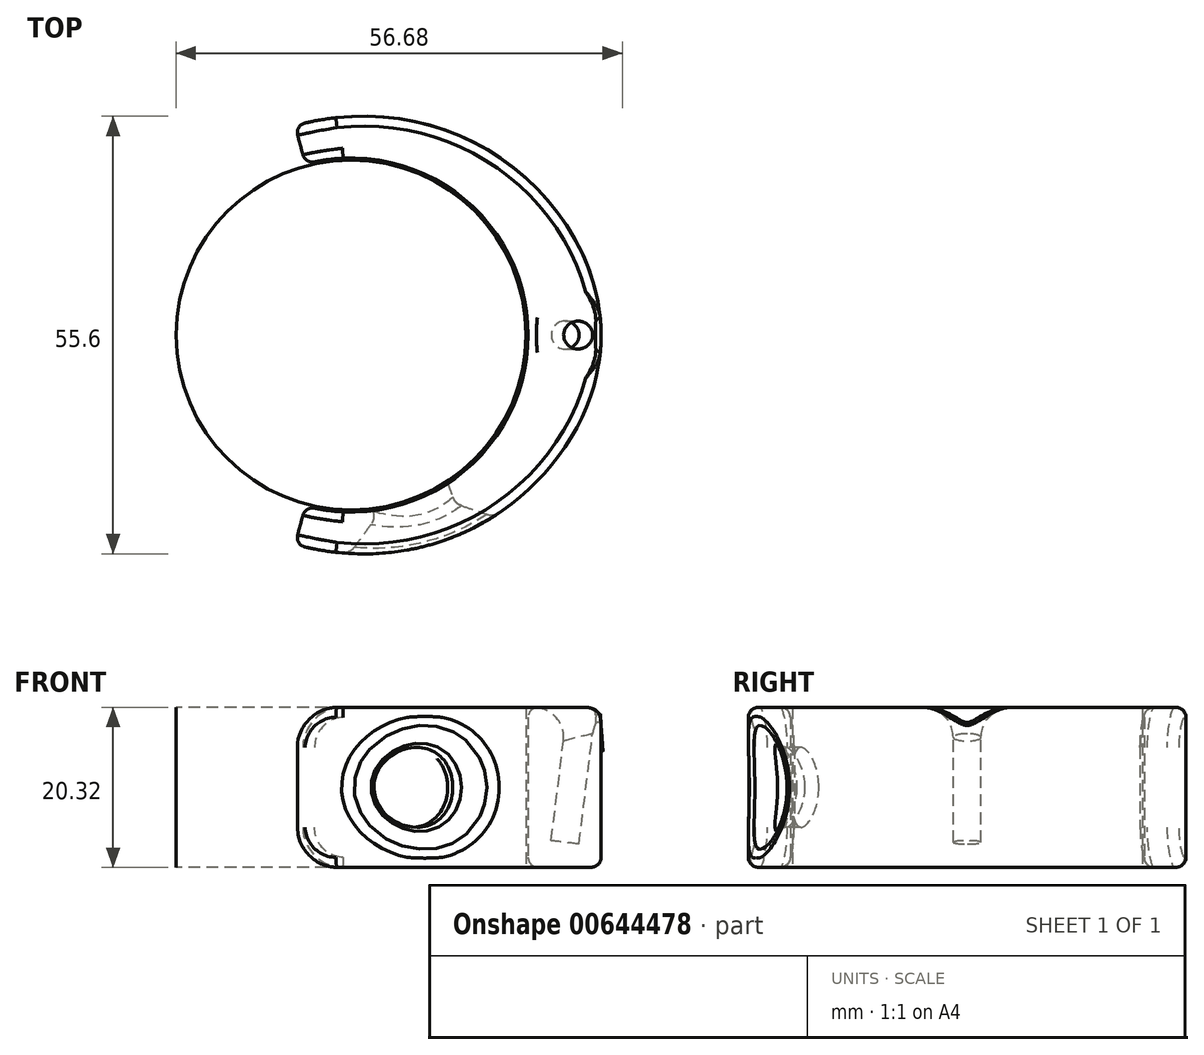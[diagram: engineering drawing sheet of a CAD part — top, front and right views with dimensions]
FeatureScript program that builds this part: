
annotation { "Feature Type Name" : "Feature", "Feature Type Description" : "" }
export const myFeature = defineFeature(function(context is Context, id is Id, definition is map)
    precondition{}
    {
        {
            var Q0;
            Q0=qCreatedBy(makeId("Top.planeOp"),FACE);
            var sketch = newSketch(context, id + "F0", { "sketchPlane" : qUnion([Q0])});
            skArc(sketch, "E0", {"start": v(-5.82, -21.71) * mm, "mid": v(22.48, 0) * mm, "end": v(-5.82, 21.71) * mm});
            skLineSegment(sketch, "E1", {"start": v(-7.13, 26.62) * mm, "end": v(-5.82, 21.71) * mm});
            skLineSegment(sketch, "E2", {"start": v(0, 0) * mm, "end": v(22.48, 0) * mm, "construction": true});
            skLineSegment(sketch, "E3.MirrorCS", {"start": v(-7.13, -26.62) * mm, "end": v(-5.82, -21.71) * mm});
            skLineSegment(sketch, "E4", {"start": v(22.48, 0) * mm, "end": v(31.75, 0) * mm, "construction": true});
            skFitSpline(sketch, "E5", {"points": [v(-7.13, 26.62) * mm, v(31.75, 0) * mm], "startDerivative": vector(65.04, 17.43) * mm, "endDerivative": vector(0, -47.29) * mm});
            skLineSegment(sketch, "E6", {"start": v(-7.13, 26.62) * mm, "end": v(-24.88, 21.87) * mm, "construction": true});
            skLineSegment(sketch, "E7", {"start": v(31.75, 0) * mm, "end": v(31.75, -8.23) * mm, "construction": true});
            skFitSpline(sketch, "E8.MirrorCS", {"points": [v(-7.13, -26.62) * mm, v(31.75, 0) * mm], "startDerivative": vector(65.04, -17.43) * mm, "endDerivative": vector(0, 47.29) * mm});
            skCircle(sketch, "E9", {"center": v(0, 0) * mm, "radius": 22.23 * mm});
            skSolve(sketch);
        }
        {
            var Q0;
            Q0 = qSketchRegion(id + "F0", true);
            extrude(context, id + "F1", {"entities" : qUnion([Q0]), "depth" : 20.32 * mm, "offsetDistance" : 25.4 * mm});
        }
        {
            var Q0;
            Q0=qCreatedBy(makeId("Front.planeOp"),FACE);
            var sketch = newSketch(context, id + "F2", { "sketchPlane" : qUnion([Q0])});
            skLineSegment(sketch, "E10", {"start": v(27.89, 23.54) * mm, "end": v(25.41, 3.4) * mm});
            skLineSegment(sketch, "E11", {"start": v(26.9, 0.89) * mm, "end": v(29.93, 25.6) * mm, "construction": true});
            skLineSegment(sketch, "E12", {"start": v(25.41, 3.4) * mm, "end": v(27.18, 3.18) * mm});
            skLineSegment(sketch, "E13", {"start": v(27.18, 3.18) * mm, "end": v(29.65, 23.32) * mm});
            skLineSegment(sketch, "E14", {"start": v(29.65, 23.32) * mm, "end": v(27.89, 23.54) * mm});
            skLineSegment(sketch, "E15", {"start": v(0, 0) * mm, "end": v(36.8, 0) * mm});
            skSolve(sketch);
        }
        {
            var Q0;
            Q0=makeQuery(id+"F2.imprint","IMPRINT",FACE,{"disambiguationData":[TD([[makeQuery(id+"F2.imprint","IMPRINT",EDGE,{"derivedFrom":sQuery(id+"F2.wireOp",EDGE,"E10")}),1.0]])]});
            var Q1;
            Q1=sQuery(id+"F2.wireOp",EDGE,"E11");
            revolve(context, id + "F3", {"operationType" : NewBodyOperationType.REMOVE, "entities" : qUnion([Q0]), "axis" : qUnion([Q1]), "revolveType" : RevolveType.FULL, "oppositeDirection" : true});
        }
        {
            var Q0;
            Q0=qCreatedBy(makeId("Top.planeOp"),FACE);
            var sketch = newSketch(context, id + "F4", { "sketchPlane" : qUnion([Q0])});
            skLineSegment(sketch, "E16", {"start": v(0, 0) * mm, "end": v(11.08, -30.43) * mm});
            skLineSegment(sketch, "E17", {"start": v(0, 0) * mm, "end": v(-26.24, 0) * mm, "construction": true});
            skSolve(sketch);
        }
        {
            var Q0;
            Q0=sQuery(id+"F4.wireOp",EDGE,"E16");
            var Q1;
            Q1=sQuery(id+"F4.wireOp",VERTEX,"E16.end");
            cPlane(context, id + "F5", {"entities" : qUnion([Q0, Q1]), "cplaneType" : CPlaneType.LINE_POINT, "offset" : 25.4 * mm, "width" : 152.4 * mm, "height" : 152.4 * mm});
        }
        {
            var Q0;
            Q0=qCreatedBy(id+"F5.planeOp",FACE);
            var sketch = newSketch(context, id + "F6", { "sketchPlane" : qUnion([Q0])});
            skCircle(sketch, "E18", {"center": v(0, 10.16) * mm, "radius": 5.08 * mm});
            skLineSegment(sketch, "E19", {"start": v(0, 10.16) * mm, "end": v(-15.8, 10.16) * mm, "construction": true});
            skLineSegment(sketch, "E20", {"start": v(0, 0) * mm, "end": v(0, 10.16) * mm, "construction": true});
            skSolve(sketch);
        }
        {
            var Q0;
            Q0 = qSketchRegion(id + "F6", true);
            var Q1;
            Q1=makeQuery(id+"F1.opExtrude","SWEPT_FACE",FACE,{"disambiguationData":[OSD([sQuery(id+"F0.wireOp",EDGE,"E0")])]});
            extrude(context, id + "F7", {"entities" : qUnion([Q0]), "operationType" : NewBodyOperationType.REMOVE, "endBound" : BoundingType.UP_TO_SURFACE, "oppositeDirection" : true, "depth" : 25.4 * mm, "endBoundEntityFace" : qUnion([Q1]), "offsetDistance" : 25.4 * mm});
        }
        {
            var Q0;
            Q0=makeQuery(id+"F1.opExtrude","CAP_EDGE",EDGE,{"disambiguationData":[OSD([sQuery(id+"F0.wireOp",EDGE,"E1")])],"isStart":false});
            var Q1;
            Q1=makeQuery(id+"F1.opExtrude","CAP_EDGE",EDGE,{"disambiguationData":[OSD([sQuery(id+"F0.wireOp",EDGE,"E1")])],"isStart":true});
            var Q2;
            Q2=makeQuery(id+"F1.opExtrude","CAP_EDGE",EDGE,{"disambiguationData":[OSD([sQuery(id+"F0.wireOp",EDGE,"E3.MirrorCS")])],"isStart":false});
            var Q3;
            Q3=makeQuery(id+"F1.opExtrude","CAP_EDGE",EDGE,{"disambiguationData":[OSD([sQuery(id+"F0.wireOp",EDGE,"E3.MirrorCS")])],"isStart":true});
            fillet(context, id + "F8", {"entities" : qUnion([Q0, Q1, Q2, Q3]), "radius" : 5.08 * mm, "tangentPropagation" : true, "rho" : .4, "crossSection" : FilletCrossSection.CONIC, "allowEdgeOverflow" : false});
        }
        {
            var Q0;
            Q0=makeQuery(id+"F1.opExtrude","CAP_EDGE",EDGE,{"disambiguationData":[OSD([sQuery(id+"F0.wireOp",EDGE,"E0")])],"isStart":false});
            var Q1;
            Q1=makeQuery(id+"F1.opExtrude","CAP_EDGE",EDGE,{"disambiguationData":[OSD([sQuery(id+"F0.wireOp",EDGE,"E8.MirrorCS")])],"isStart":false});
            fillet(context, id + "F9", {"entities" : qUnion([Q0, Q1]), "radius" : 1.27 * mm, "tangentPropagation" : true, "allowEdgeOverflow" : false});
        }
        {
            var Q0;
            Q0=makeQuery(id+"F3.boolean.opBoolean","INTERSECT",EDGE,{"derivedFrom":[makeQuery(id+"F1.opExtrude","CAP_FACE",FACE,{"disambiguationData":[OSD([sQuery(id+"F0.wireOp",EDGE,"E0"),sQuery(id+"F0.wireOp",EDGE,"E1"),sQuery(id+"F0.wireOp",EDGE,"E3.MirrorCS"),sQuery(id+"F0.wireOp",EDGE,"E5"),sQuery(id+"F0.wireOp",EDGE,"E8.MirrorCS")])],"isStart":false}),makeQuery(id+"F3.opRevolve","SWEPT_FACE",FACE,{"disambiguationData":[OSD([sQuery(id+"F2.wireOp",EDGE,"E10")])]})]});
            fillet(context, id + "F10", {"entities" : qUnion([Q0]), "radius" : 3.8 * mm, "allowEdgeOverflow" : false});
        }
        {
            var Q0;
            {var subQ0=sQuery(id+"F0.wireOp",EDGE,"E5");Q0=makeQuery(id+"F10.opFillet","BLEND_EDGE",EDGE,{"blendedFrom":[makeQuery(id+"F3.boolean.opBoolean","INTERSECT",EDGE,{"derivedFrom":[makeQuery(id+"F1.opExtrude","CAP_FACE",FACE,{"disambiguationData":[OSD([sQuery(id+"F0.wireOp",EDGE,"E0"),sQuery(id+"F0.wireOp",EDGE,"E1"),sQuery(id+"F0.wireOp",EDGE,"E3.MirrorCS"),subQ0,sQuery(id+"F0.wireOp",EDGE,"E8.MirrorCS")])],"isStart":false}),makeQuery(id+"F3.opRevolve","SWEPT_FACE",FACE,{"disambiguationData":[OSD([sQuery(id+"F2.wireOp",EDGE,"E10")])]})]}),makeQuery(id+"F9.opFillet","BLEND_FACE",FACE,{"disambiguationData":[OSD([subQ0]),TDD([makeQuery(id+"F1.opExtrude","CAP_EDGE",EDGE,{"disambiguationData":[OSD([subQ0])],"isStart":false})])]})],"blendedInto":[makeQuery(id+"F9.opFillet","BLEND_FACE",FACE,{"disambiguationData":[OSD([subQ0]),TDD([makeQuery(id+"F1.opExtrude","CAP_EDGE",EDGE,{"disambiguationData":[OSD([subQ0])],"isStart":false})])]})]});}
            var Q1;
            {var subQ0=sQuery(id+"F0.wireOp",EDGE,"E8.MirrorCS");Q1=makeQuery(id+"F10.opFillet","BLEND_EDGE",EDGE,{"blendedFrom":[makeQuery(id+"F3.boolean.opBoolean","INTERSECT",EDGE,{"derivedFrom":[makeQuery(id+"F1.opExtrude","CAP_FACE",FACE,{"disambiguationData":[OSD([sQuery(id+"F0.wireOp",EDGE,"E0"),sQuery(id+"F0.wireOp",EDGE,"E1"),sQuery(id+"F0.wireOp",EDGE,"E3.MirrorCS"),sQuery(id+"F0.wireOp",EDGE,"E5"),subQ0])],"isStart":false}),makeQuery(id+"F3.opRevolve","SWEPT_FACE",FACE,{"disambiguationData":[OSD([sQuery(id+"F2.wireOp",EDGE,"E10")])]})]}),makeQuery(id+"F9.opFillet","BLEND_FACE",FACE,{"disambiguationData":[OSD([subQ0]),TDD([makeQuery(id+"F1.opExtrude","CAP_EDGE",EDGE,{"disambiguationData":[OSD([subQ0])],"isStart":false})])]})],"blendedInto":[makeQuery(id+"F9.opFillet","BLEND_FACE",FACE,{"disambiguationData":[OSD([subQ0]),TDD([makeQuery(id+"F1.opExtrude","CAP_EDGE",EDGE,{"disambiguationData":[OSD([subQ0])],"isStart":false})])]})]});}
            fillet(context, id + "F11", {"entities" : qUnion([Q0, Q1]), "radius" : 0.38 * mm, "tangentPropagation" : true, "allowEdgeOverflow" : false});
        }
        {
            var Q0;
            Q0=makeQuery(id+"FVZt6SSctKpJtOL_108.3.F7.boolean.opBoolean","INTERSECT",EDGE,{"derivedFrom":[makeQuery(id+"F1.opExtrude","SWEPT_FACE",FACE,{"disambiguationData":[OSD([sQuery(id+"F0.wireOp",EDGE,"E5")])]}),makeQuery(id+"FVZt6SSctKpJtOL_108.3.F7.opExtrude","SWEPT_FACE",FACE,{"disambiguationData":[OSD([sQuery(id+"F6.wireOp",EDGE,"E18")])]})]});
            var Q1;
            Q1=makeQuery(id+"FVZt6SSctKpJtOL_108.2.F7.boolean.opBoolean","INTERSECT",EDGE,{"derivedFrom":[makeQuery(id+"F1.opExtrude","SWEPT_FACE",FACE,{"disambiguationData":[OSD([sQuery(id+"F0.wireOp",EDGE,"E5")])]}),makeQuery(id+"FVZt6SSctKpJtOL_108.2.F7.opExtrude","SWEPT_FACE",FACE,{"disambiguationData":[OSD([sQuery(id+"F6.wireOp",EDGE,"E18")])]})]});
            var Q2;
            Q2=makeQuery(id+"FVZt6SSctKpJtOL_108.1.F7.boolean.opBoolean","INTERSECT",EDGE,{"derivedFrom":[makeQuery(id+"F1.opExtrude","SWEPT_FACE",FACE,{"disambiguationData":[OSD([sQuery(id+"F0.wireOp",EDGE,"E8.MirrorCS")])]}),makeQuery(id+"FVZt6SSctKpJtOL_108.1.F7.opExtrude","SWEPT_FACE",FACE,{"disambiguationData":[OSD([sQuery(id+"F6.wireOp",EDGE,"E18")])]})]});
            var Q3;
            Q3=makeQuery(id+"F7.boolean.opBoolean","INTERSECT",EDGE,{"derivedFrom":[makeQuery(id+"F1.opExtrude","SWEPT_FACE",FACE,{"disambiguationData":[OSD([sQuery(id+"F0.wireOp",EDGE,"E8.MirrorCS")])]}),makeQuery(id+"F7.opExtrude","SWEPT_FACE",FACE,{"disambiguationData":[OSD([sQuery(id+"F6.wireOp",EDGE,"E18")])]})]});
            chamfer(context, id + "F12", {"entities" : qUnion([Q0, Q1, Q2, Q3]), "width" : 3.3 * mm, "tangentPropagation" : true});
        }
        {
            var Q0;
            {var subQ0=sQuery(id+"F6.wireOp",EDGE,"E18");var subQ1=sQuery(id+"F0.wireOp",EDGE,"E5");Q0=makeQuery(id+"F12.opChamfer","BLEND_FACE",FACE,{"disambiguationData":[OSD([subQ1,subQ0]),TDD([makeQuery(id+"FVZt6SSctKpJtOL_108.2.F7.boolean.opBoolean","INTERSECT",EDGE,{"derivedFrom":[makeQuery(id+"F1.opExtrude","SWEPT_FACE",FACE,{"disambiguationData":[OSD([subQ1])]}),makeQuery(id+"FVZt6SSctKpJtOL_108.2.F7.opExtrude","SWEPT_FACE",FACE,{"disambiguationData":[OSD([subQ0])]})]})])]});}
            var Q1;
            {var subQ0=sQuery(id+"F6.wireOp",EDGE,"E18");var subQ1=sQuery(id+"F0.wireOp",EDGE,"E8.MirrorCS");Q1=makeQuery(id+"F12.opChamfer","BLEND_FACE",FACE,{"disambiguationData":[OSD([subQ1,subQ0]),TDD([makeQuery(id+"FVZt6SSctKpJtOL_108.1.F7.boolean.opBoolean","INTERSECT",EDGE,{"derivedFrom":[makeQuery(id+"F1.opExtrude","SWEPT_FACE",FACE,{"disambiguationData":[OSD([subQ1])]}),makeQuery(id+"FVZt6SSctKpJtOL_108.1.F7.opExtrude","SWEPT_FACE",FACE,{"disambiguationData":[OSD([subQ0])]})]})])]});}
            var Q2;
            {var subQ0=sQuery(id+"F6.wireOp",EDGE,"E18");var subQ1=sQuery(id+"F0.wireOp",EDGE,"E5");Q2=makeQuery(id+"F12.opChamfer","BLEND_FACE",FACE,{"disambiguationData":[OSD([subQ1,subQ0]),TDD([makeQuery(id+"FVZt6SSctKpJtOL_108.3.F7.boolean.opBoolean","INTERSECT",EDGE,{"derivedFrom":[makeQuery(id+"F1.opExtrude","SWEPT_FACE",FACE,{"disambiguationData":[OSD([subQ1])]}),makeQuery(id+"FVZt6SSctKpJtOL_108.3.F7.opExtrude","SWEPT_FACE",FACE,{"disambiguationData":[OSD([subQ0])]})]})])]});}
            var Q3;
            {var subQ0=sQuery(id+"F6.wireOp",EDGE,"E18");var subQ1=sQuery(id+"F0.wireOp",EDGE,"E8.MirrorCS");Q3=makeQuery(id+"F12.opChamfer","BLEND_FACE",FACE,{"disambiguationData":[OSD([subQ1,subQ0]),TDD([makeQuery(id+"F7.boolean.opBoolean","INTERSECT",EDGE,{"derivedFrom":[makeQuery(id+"F1.opExtrude","SWEPT_FACE",FACE,{"disambiguationData":[OSD([subQ1])]}),makeQuery(id+"F7.opExtrude","SWEPT_FACE",FACE,{"disambiguationData":[OSD([subQ0])]})]})])]});}
            fillet(context, id + "F13", {"entities" : qUnion([Q0, Q1, Q2, Q3]), "radius" : 1.78 * mm, "tangentPropagation" : true, "allowEdgeOverflow" : false});
        }
    });
